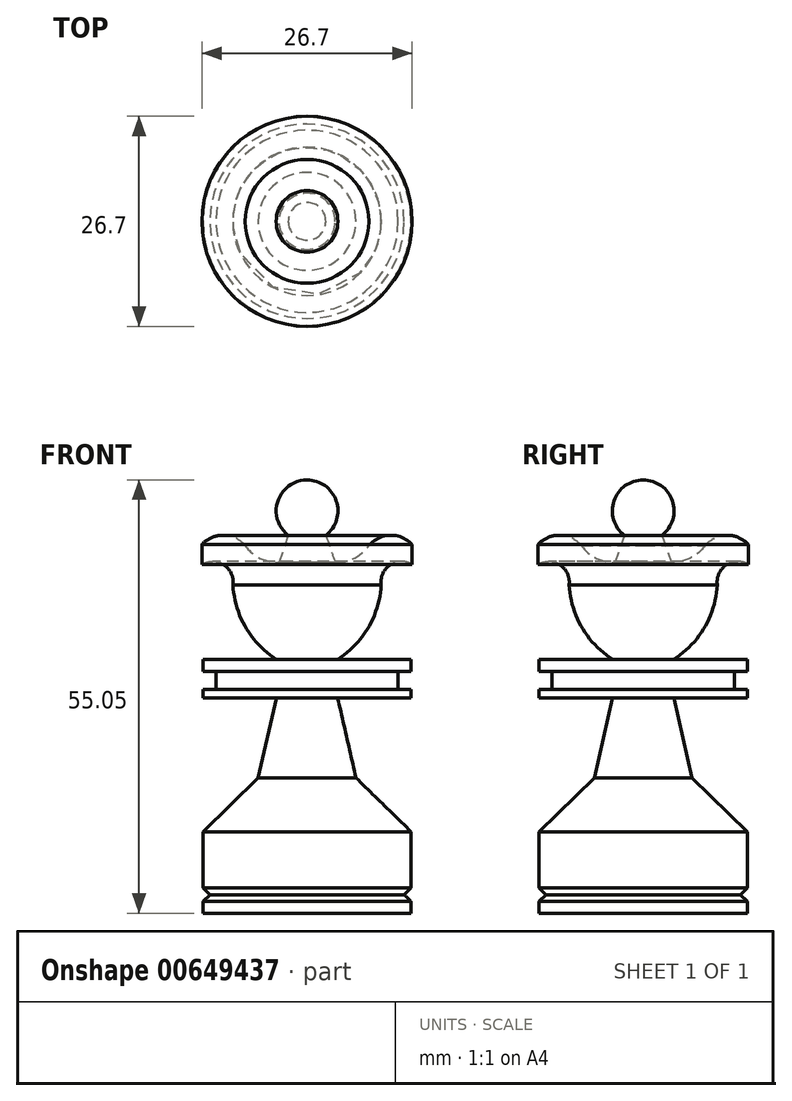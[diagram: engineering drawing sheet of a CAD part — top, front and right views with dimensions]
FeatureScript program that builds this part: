
annotation { "Feature Type Name" : "Feature", "Feature Type Description" : "" }
export const myFeature = defineFeature(function(context is Context, id is Id, definition is map)
    precondition{}
    {
        {
            var Q0;
            Q0=qCreatedBy(makeId("Front.planeOp"),FACE);
            var sketch = newSketch(context, id + "F0", { "sketchPlane" : qUnion([Q0])});
            skLineSegment(sketch, "E0", {"start": v(0, 0) * mm, "end": v(-13.21, 0) * mm});
            skLineSegment(sketch, "E1", {"start": v(-13.21, 0) * mm, "end": v(-13.21, 1.5) * mm});
            skLineSegment(sketch, "E2", {"start": v(0, 0) * mm, "end": v(0, 2.37) * mm});
            skLineSegment(sketch, "E3", {"start": v(-13.21, 1.5) * mm, "end": v(-12.35, 2.37) * mm});
            skLineSegment(sketch, "E4", {"start": v(-12.35, 2.37) * mm, "end": v(-13.22, 3.23) * mm});
            skLineSegment(sketch, "E5", {"start": v(-13.22, 3.23) * mm, "end": v(-13.22, 10.36) * mm});
            skLineSegment(sketch, "E6", {"start": v(-13.22, 10.36) * mm, "end": v(-6.21, 17.2) * mm});
            skLineSegment(sketch, "E7", {"start": v(-6.21, 17.2) * mm, "end": v(-3.88, 27.38) * mm});
            skLineSegment(sketch, "E8", {"start": v(-3.88, 27.38) * mm, "end": v(-13.22, 27.38) * mm});
            skLineSegment(sketch, "E9", {"start": v(-13.22, 27.38) * mm, "end": v(-13.22, 28.44) * mm});
            skLineSegment(sketch, "E10", {"start": v(-13.22, 28.44) * mm, "end": v(-11.57, 28.44) * mm});
            skLineSegment(sketch, "E11", {"start": v(-11.57, 28.44) * mm, "end": v(-11.57, 30.73) * mm});
            skLineSegment(sketch, "E12", {"start": v(-11.57, 30.73) * mm, "end": v(-13.22, 30.73) * mm});
            skLineSegment(sketch, "E13", {"start": v(-13.22, 30.73) * mm, "end": v(-13.22, 32.23) * mm});
            skLineSegment(sketch, "E14", {"start": v(-13.22, 32.23) * mm, "end": v(-3.87, 32.23) * mm});
            skArc(sketch, "E15", {"start": v(-9.42, 41.72) * mm, "mid": v(-7.78, 36.3) * mm, "end": v(-3.87, 32.23) * mm});
            skArc(sketch, "E16", {"start": v(-9.42, 41.72) * mm, "mid": v(-10.56, 44.26) * mm, "end": v(-13.35, 44.34) * mm});
            skLineSegment(sketch, "E17", {"start": v(-13.35, 44.34) * mm, "end": v(-13.35, 47.2) * mm});
            skArc(sketch, "E18", {"start": v(-7.87, 46.72) * mm, "mid": v(-10.57, 48.02) * mm, "end": v(-13.35, 46.87) * mm});
            skArc(sketch, "E19", {"start": v(-7.87, 46.72) * mm, "mid": v(-5.99, 45.11) * mm, "end": v(-3.57, 44.58) * mm});
            skLineSegment(sketch, "E20", {"start": v(-3.57, 44.58) * mm, "end": v(-2.4, 48.02) * mm});
            skPoint(sketch, "E20.endSnap0", {"position": v(-10.57, 48.02) * mm});
            skArc(sketch, "E21", {"start": v(-2.4, 48.02) * mm, "mid": v(-3.71, 52.39) * mm, "end": v(0, 55.05) * mm});
            skLineSegment(sketch, "E22", {"start": v(0, 55.05) * mm, "end": v(0, 0) * mm});
            skSolve(sketch);
        }
        {
            var Q0;
            {var subQ0=sQuery(id+"F0.wireOp",EDGE,"E0");Q0=makeQuery(id+"F0.imprint","IMPRINT",FACE,{"disambiguationData":[TD([[makeQuery(id+"F0.imprint","IMPRINT",EDGE,{"derivedFrom":subQ0}),-1.0]])]});}
            var Q1;
            Q1=sQuery(id+"F0.wireOp",EDGE,"E22");
            revolve(context, id + "F1", {"entities" : qUnion([Q0]), "axis" : qUnion([Q1]), "revolveType" : RevolveType.FULL});
        }
    });
